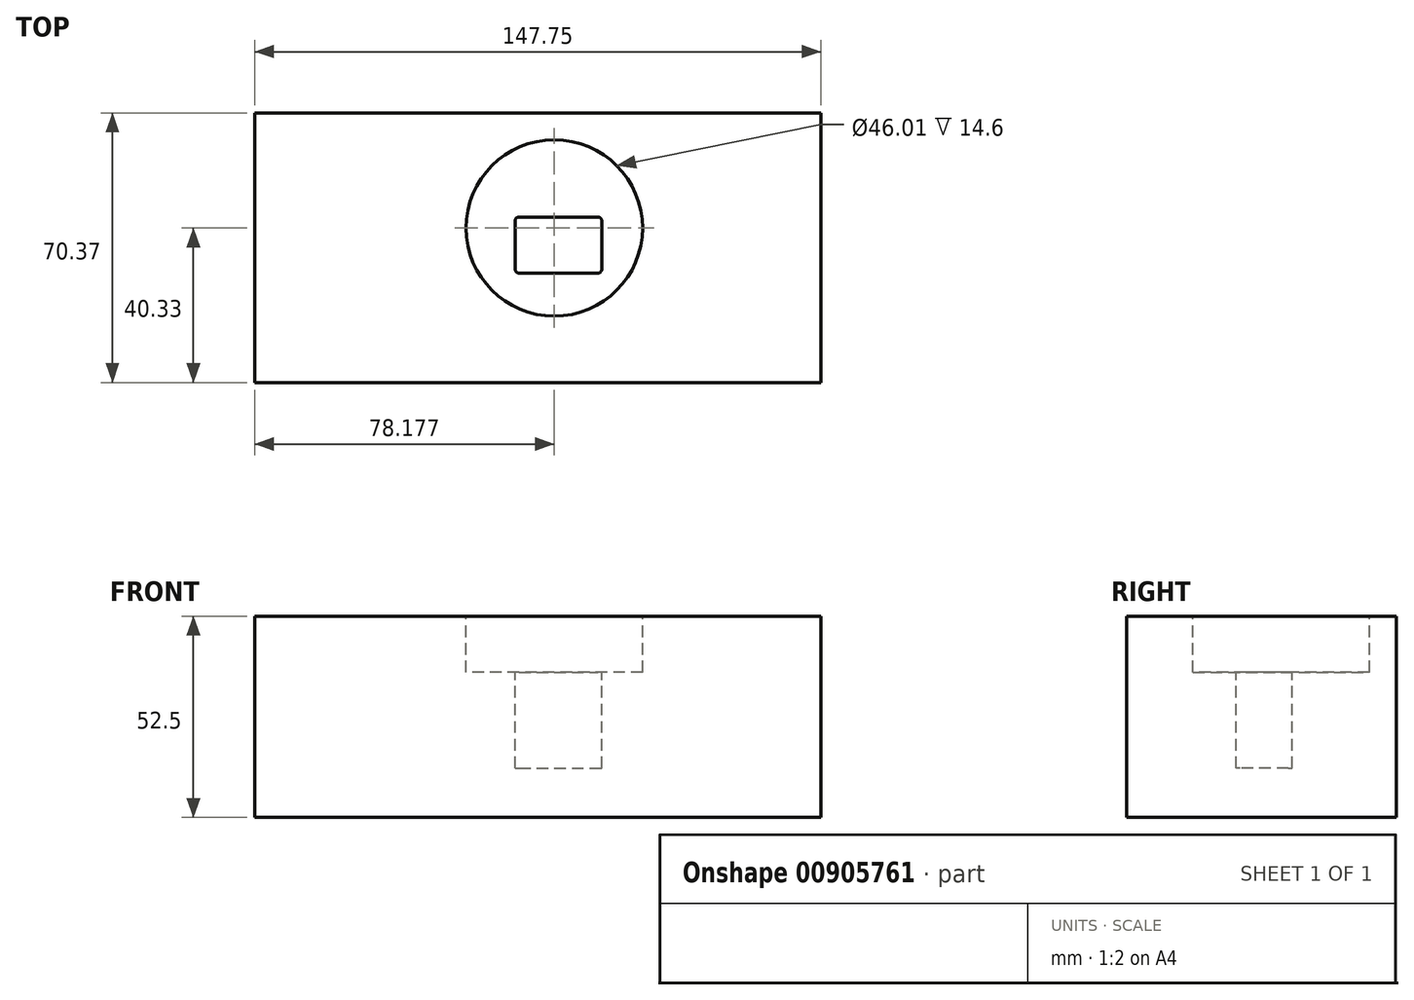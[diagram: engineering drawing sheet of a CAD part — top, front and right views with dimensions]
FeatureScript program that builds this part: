
annotation { "Feature Type Name" : "Feature", "Feature Type Description" : "" }
export const myFeature = defineFeature(function(context is Context, id is Id, definition is map)
    precondition{}
    {
        {
            var Q0;
            Q0=qCreatedBy(makeId("Top.planeOp"),FACE);
            var sketch = newSketch(context, id + "F0", { "sketchPlane" : qUnion([Q0])});
            skLineSegment(sketch, "E0.bottom", {"start": v(-65.5, 27.17) * mm, "end": v(82.25, 27.17) * mm});
            skLineSegment(sketch, "E0.top", {"start": v(-65.5, -43.2) * mm, "end": v(82.25, -43.2) * mm});
            skLineSegment(sketch, "E0.left", {"start": v(-65.5, 27.17) * mm, "end": v(-65.5, -43.2) * mm});
            skLineSegment(sketch, "E0.right", {"start": v(82.25, 27.17) * mm, "end": v(82.25, -43.2) * mm});
            skSolve(sketch);
        }
        {
            var Q0;
            Q0 = qSketchRegion(id + "F0", true);
            extrude(context, id + "F1", {"entities" : qUnion([Q0]), "depth" : 52.5 * mm, "offsetDistance" : 25 * mm});
        }
        {
            var Q0;
            Q0=makeQuery(id+"F1.opExtrude","CAP_FACE",FACE,{"disambiguationData":[OSD([sQuery(id+"F0.wireOp",EDGE,"E0.bottom"),sQuery(id+"F0.wireOp",EDGE,"E0.top"),sQuery(id+"F0.wireOp",EDGE,"E0.left"),sQuery(id+"F0.wireOp",EDGE,"E0.right")])],"isStart":false});
            var sketch = newSketch(context, id + "F2", { "sketchPlane" : qUnion([Q0])});
            skCircle(sketch, "E1", {"center": v(12.68, -2.87) * mm, "radius": 23 * mm});
            skSolve(sketch);
        }
        {
            var Q0;
            Q0 = qSketchRegion(id + "F2", true);
            extrude(context, id + "F3", {"entities" : qUnion([Q0]), "operationType" : NewBodyOperationType.REMOVE, "oppositeDirection" : true, "depth" : 14.6 * mm, "offsetDistance" : 25 * mm});
        }
        {
            var Q0;
            Q0=makeQuery(id+"F3.boolean.opBoolean","COPY",FACE,{"derivedFrom":makeQuery(id+"F3.opExtrude","CAP_FACE",FACE,{"disambiguationData":[OSD([sQuery(id+"F2.wireOp",EDGE,"E1")])],"isStart":false})});
            var sketch = newSketch(context, id + "F4", { "sketchPlane" : qUnion([Q0])});
            skLineSegment(sketch, "E2.bottom", {"start": v(3.49, 0) * mm, "end": v(24.04, 0) * mm});
            skLineSegment(sketch, "E2.top", {"start": v(3.49, -14.65) * mm, "end": v(24.04, -14.65) * mm});
            skLineSegment(sketch, "E2.left", {"start": v(2.49, -1) * mm, "end": v(2.49, -13.65) * mm});
            skLineSegment(sketch, "E2.right", {"start": v(25.04, -1) * mm, "end": v(25.04, -13.65) * mm});
            skPoint(sketch, "E3.visualSharp", {"position": v(2.49, 0) * mm});
            skArc(sketch, "E3.filletArc", {"start": v(3.49, 0) * mm, "mid": v(2.78, -0.3) * mm, "end": v(2.49, -1) * mm});
            skPoint(sketch, "E4.visualSharp", {"position": v(2.49, -14.65) * mm});
            skArc(sketch, "E4.filletArc", {"start": v(2.49, -13.65) * mm, "mid": v(2.78, -14.35) * mm, "end": v(3.49, -14.65) * mm});
            skPoint(sketch, "E5.visualSharp", {"position": v(25.04, -14.65) * mm});
            skArc(sketch, "E5.filletArc", {"start": v(24.04, -14.65) * mm, "mid": v(24.75, -14.35) * mm, "end": v(25.04, -13.65) * mm});
            skPoint(sketch, "E6.visualSharp", {"position": v(25.04, 0) * mm});
            skArc(sketch, "E6.filletArc", {"start": v(25.04, -1) * mm, "mid": v(24.75, -0.3) * mm, "end": v(24.04, 0) * mm});
            skSolve(sketch);
        }
        {
            var Q0;
            Q0=makeQuery(id+"F4.imprint","IMPRINT",FACE,{"disambiguationData":[TD([[makeQuery(id+"F4.imprint","IMPRINT",EDGE,{"derivedFrom":sQuery(id+"F4.wireOp",EDGE,"E2.bottom")}),-1.0]])]});
            extrude(context, id + "F5", {"entities" : qUnion([Q0]), "operationType" : NewBodyOperationType.REMOVE, "oppositeDirection" : true, "depth" : 25 * mm, "offsetDistance" : 25 * mm});
        }
    });
